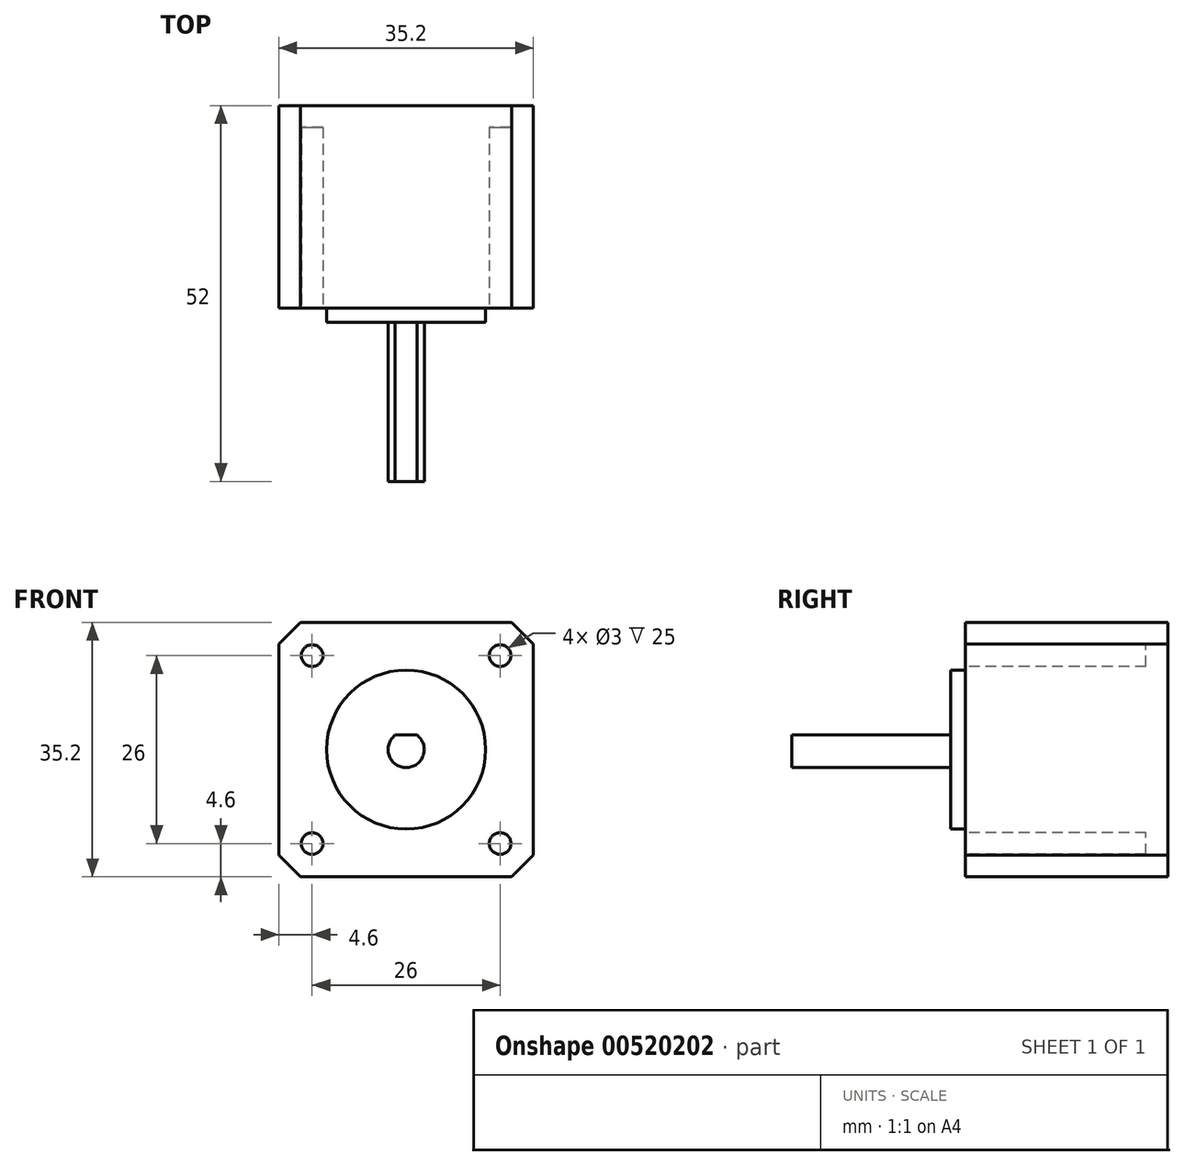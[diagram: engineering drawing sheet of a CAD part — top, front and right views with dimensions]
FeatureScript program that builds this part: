
annotation { "Feature Type Name" : "Feature", "Feature Type Description" : "" }
export const myFeature = defineFeature(function(context is Context, id is Id, definition is map)
    precondition{}
    {
        {
            var Q0;
            Q0=qCreatedBy(makeId("Front.planeOp"),FACE);
            var sketch = newSketch(context, id + "F0", { "sketchPlane" : qUnion([Q0])});
            skLineSegment(sketch, "E0.bottom", {"start": v(-17.6, 17.6) * mm, "end": v(17.6, 17.6) * mm});
            skLineSegment(sketch, "E0.top", {"start": v(-17.6, -17.6) * mm, "end": v(17.6, -17.6) * mm});
            skLineSegment(sketch, "E0.left", {"start": v(-17.6, 17.6) * mm, "end": v(-17.6, -17.6) * mm});
            skLineSegment(sketch, "E0.right", {"start": v(17.6, 17.6) * mm, "end": v(17.6, -17.6) * mm});
            skPoint(sketch, "E0.middle", {"position": v(0, 0) * mm});
            skSolve(sketch);
        }
        {
            var Q0;
            Q0 = qSketchRegion(id + "F0", true);
            extrude(context, id + "F1", {"entities" : qUnion([Q0]), "depth" : 28 * mm, "offsetDistance" : 25 * mm});
        }
        {
            var Q0;
            Q0=makeQuery(id+"F1.opExtrude","SWEPT_EDGE",EDGE,{"disambiguationData":[OSD([sQuery(id+"F0.wireOp",EDGE,"E0.bottom"),sQuery(id+"F0.wireOp",EDGE,"E0.left")])]});
            var Q1;
            Q1=makeQuery(id+"F1.opExtrude","SWEPT_EDGE",EDGE,{"disambiguationData":[OSD([sQuery(id+"F0.wireOp",EDGE,"E0.top"),sQuery(id+"F0.wireOp",EDGE,"E0.left")])]});
            var Q2;
            Q2=makeQuery(id+"F1.opExtrude","SWEPT_EDGE",EDGE,{"disambiguationData":[OSD([sQuery(id+"F0.wireOp",EDGE,"E0.top"),sQuery(id+"F0.wireOp",EDGE,"E0.right")])]});
            var Q3;
            Q3=makeQuery(id+"F1.opExtrude","SWEPT_EDGE",EDGE,{"disambiguationData":[OSD([sQuery(id+"F0.wireOp",EDGE,"E0.bottom"),sQuery(id+"F0.wireOp",EDGE,"E0.right")])]});
            chamfer(context, id + "F2", {"entities" : qUnion([Q0, Q1, Q2, Q3]), "width" : 3 * mm, "tangentPropagation" : true});
        }
        {
            var Q0;
            Q0=makeQuery(id+"F1.opExtrude","CAP_FACE",FACE,{"disambiguationData":[OSD([sQuery(id+"F0.wireOp",EDGE,"E0.bottom"),sQuery(id+"F0.wireOp",EDGE,"E0.top"),sQuery(id+"F0.wireOp",EDGE,"E0.left"),sQuery(id+"F0.wireOp",EDGE,"E0.right")])],"isStart":false});
            var sketch = newSketch(context, id + "F3", { "sketchPlane" : qUnion([Q0])});
            skArc(sketch, "E1", {"start": v(-1.5, 2) * mm, "mid": v(0, -2.5) * mm, "end": v(1.5, 2) * mm});
            skLineSegment(sketch, "E2", {"start": v(-1.5, 2) * mm, "end": v(1.5, 2) * mm});
            skLineSegment(sketch, "E3", {"start": v(0, 2) * mm, "end": v(0, -2.5) * mm, "construction": true});
            skSolve(sketch);
        }
        {
            var Q0;
            Q0 = qSketchRegion(id + "F3", true);
            extrude(context, id + "F4", {"entities" : qUnion([Q0]), "operationType" : NewBodyOperationType.ADD, "depth" : 24 * mm, "offsetDistance" : 25 * mm});
        }
        {
            var Q0;
            Q0=makeQuery(id+"F1.opExtrude","CAP_FACE",FACE,{"disambiguationData":[OSD([sQuery(id+"F0.wireOp",EDGE,"E0.bottom"),sQuery(id+"F0.wireOp",EDGE,"E0.top"),sQuery(id+"F0.wireOp",EDGE,"E0.left"),sQuery(id+"F0.wireOp",EDGE,"E0.right")])],"isStart":false});
            var sketch = newSketch(context, id + "F5", { "sketchPlane" : qUnion([Q0])});
            skCircle(sketch, "E4", {"center": v(0, 0) * mm, "radius": 11 * mm});
            skSolve(sketch);
        }
        {
            var Q0;
            Q0 = qSketchRegion(id + "F5", true);
            extrude(context, id + "F6", {"entities" : qUnion([Q0]), "operationType" : NewBodyOperationType.ADD, "depth" : 2 * mm, "offsetDistance" : 25 * mm});
        }
        {
            var Q0;
            Q0=makeQuery(id+"F1.opExtrude","CAP_FACE",FACE,{"disambiguationData":[OSD([sQuery(id+"F0.wireOp",EDGE,"E0.bottom"),sQuery(id+"F0.wireOp",EDGE,"E0.top"),sQuery(id+"F0.wireOp",EDGE,"E0.left"),sQuery(id+"F0.wireOp",EDGE,"E0.right")])],"isStart":false});
            var sketch = newSketch(context, id + "F7", { "sketchPlane" : qUnion([Q0])});
            skLineSegment(sketch, "E5.bottom", {"start": v(-13, 13) * mm, "end": v(13, 13) * mm, "construction": true});
            skLineSegment(sketch, "E5.top", {"start": v(-13, -13) * mm, "end": v(13, -13) * mm, "construction": true});
            skLineSegment(sketch, "E5.left", {"start": v(-13, 13) * mm, "end": v(-13, -13) * mm, "construction": true});
            skLineSegment(sketch, "E5.right", {"start": v(13, 13) * mm, "end": v(13, -13) * mm, "construction": true});
            skPoint(sketch, "E5.middle", {"position": v(0, 0) * mm});
            skCircle(sketch, "E6", {"center": v(-13, 13) * mm, "radius": 1.5 * mm});
            skCircle(sketch, "E7", {"center": v(13, 13) * mm, "radius": 1.5 * mm});
            skCircle(sketch, "E8", {"center": v(13, -13) * mm, "radius": 1.5 * mm});
            skCircle(sketch, "E9", {"center": v(-13, -13) * mm, "radius": 1.5 * mm});
            skSolve(sketch);
        }
        {
            var Q0;
            Q0 = qSketchRegion(id + "F7", true);
            extrude(context, id + "F8", {"entities" : qUnion([Q0]), "operationType" : NewBodyOperationType.REMOVE, "oppositeDirection" : true, "depth" : 25 * mm, "offsetDistance" : 25 * mm});
        }
    });
